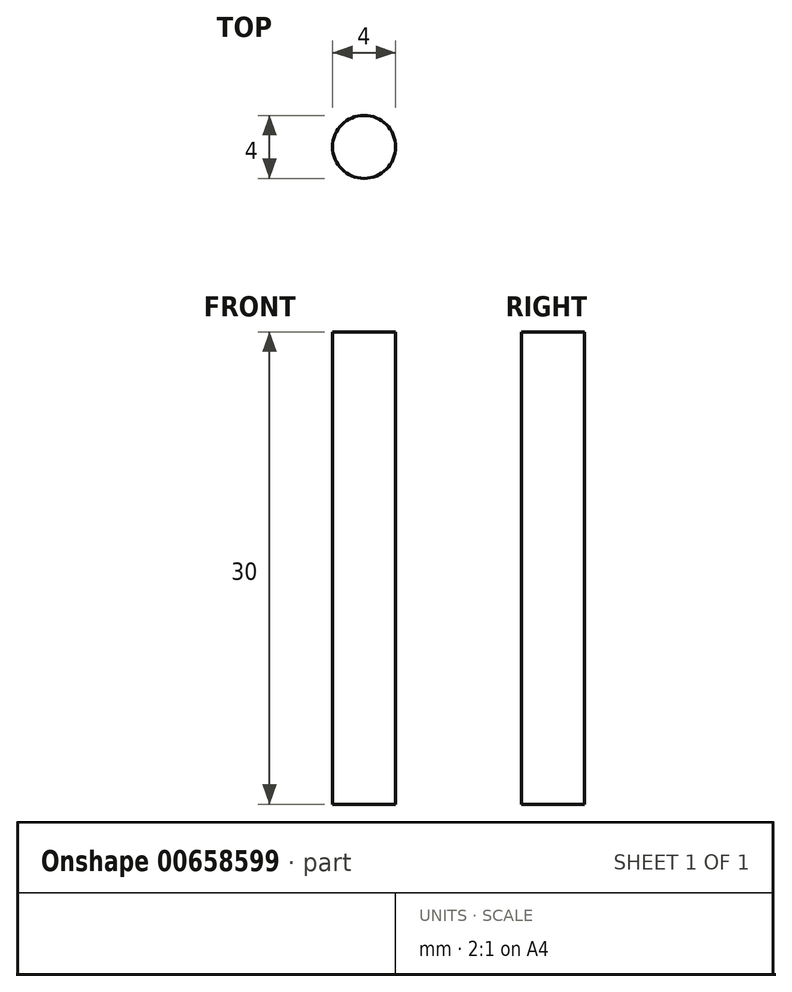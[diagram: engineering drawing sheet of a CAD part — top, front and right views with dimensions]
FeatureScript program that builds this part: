
annotation { "Feature Type Name" : "Feature", "Feature Type Description" : "" }
export const myFeature = defineFeature(function(context is Context, id is Id, definition is map)
    precondition{}
    {
        {
            var Q0;
            Q0=qCreatedBy(makeId("Top.planeOp"),FACE);
            var sketch = newSketch(context, id + "F0", { "sketchPlane" : qUnion([Q0])});
            skCircle(sketch, "E0", {"center": v(0, 0) * mm, "radius": 2 * mm});
            skSolve(sketch);
        }
        {
            var Q0;
            Q0=makeQuery(id+"F0.imprint","IMPRINT",FACE,{"disambiguationData":[TD([[makeQuery(id+"F0.imprint","IMPRINT",EDGE,{"derivedFrom":sQuery(id+"F0.wireOp",EDGE,"E0")}),1.0]])]});
            extrude(context, id + "F1", {"entities" : qUnion([Q0]), "depth" : 30 * mm, "offsetDistance" : 25 * mm});
        }
    });
